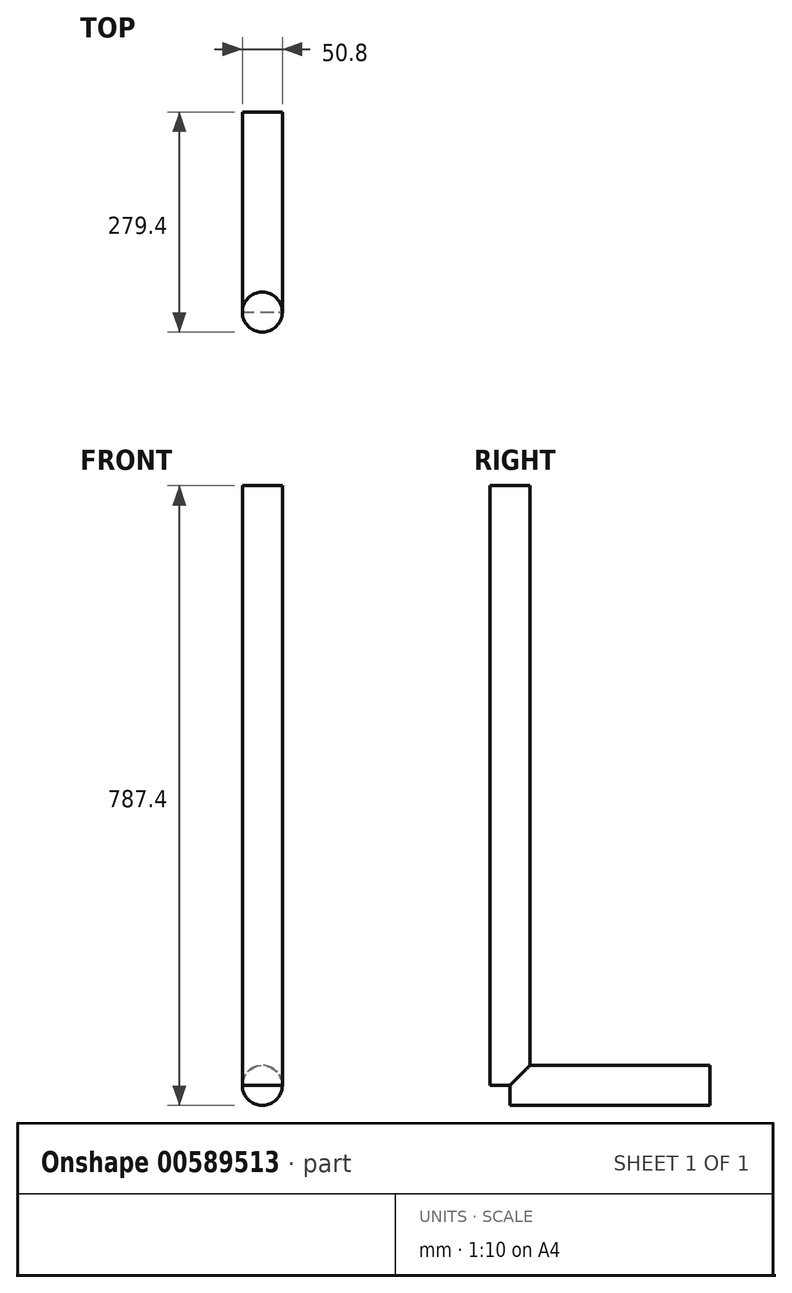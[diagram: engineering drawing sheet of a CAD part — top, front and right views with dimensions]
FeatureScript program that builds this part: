
annotation { "Feature Type Name" : "Feature", "Feature Type Description" : "" }
export const myFeature = defineFeature(function(context is Context, id is Id, definition is map)
    precondition{}
    {
        {
            var Q0;
            Q0=qCreatedBy(makeId("Top.planeOp"),FACE);
            var sketch = newSketch(context, id + "F0", { "sketchPlane" : qUnion([Q0])});
            skCircle(sketch, "E0", {"center": v(0, 0) * mm, "radius": 25.4 * mm});
            skSolve(sketch);
        }
        {
            var Q0;
            Q0=makeQuery(id+"F0.imprint","IMPRINT",FACE,{"disambiguationData":[TD([[makeQuery(id+"F0.imprint","IMPRINT",EDGE,{"derivedFrom":sQuery(id+"F0.wireOp",EDGE,"E0")}),1.0]])]});
            extrude(context, id + "F1", {"entities" : qUnion([Q0]), "depth" : 762 * mm, "offsetDistance" : 25.4 * mm});
        }
        {
            var Q0;
            Q0=qCreatedBy(makeId("Front.planeOp"),FACE);
            var sketch = newSketch(context, id + "F2", { "sketchPlane" : qUnion([Q0])});
            skCircle(sketch, "E1", {"center": v(0, 0) * mm, "radius": 25.4 * mm});
            skSolve(sketch);
        }
        {
            var Q0;
            Q0=sQuery(id+"F2.wireOp",EDGE,"E1");
            extrude(context, id + "F3", {"bodyType" : ToolBodyType.SURFACE, "surfaceEntities" : qUnion([Q0]), "depth" : 254 * mm, "offsetDistance" : 25.4 * mm});
        }
        {
            var Q0;
            Q0=qCreatedBy(makeId("Front.planeOp"),FACE);
            var sketch = newSketch(context, id + "F4", { "sketchPlane" : qUnion([Q0])});
            skCircle(sketch, "E2", {"center": v(0, 0) * mm, "radius": 25.4 * mm});
            skSolve(sketch);
        }
        {
            var Q0;
            Q0 = qSketchRegion(id + "F4", true);
            extrude(context, id + "F5", {"entities" : qUnion([Q0]), "operationType" : NewBodyOperationType.ADD, "depth" : -254 * mm, "offsetDistance" : 25.4 * mm});
        }
    });
